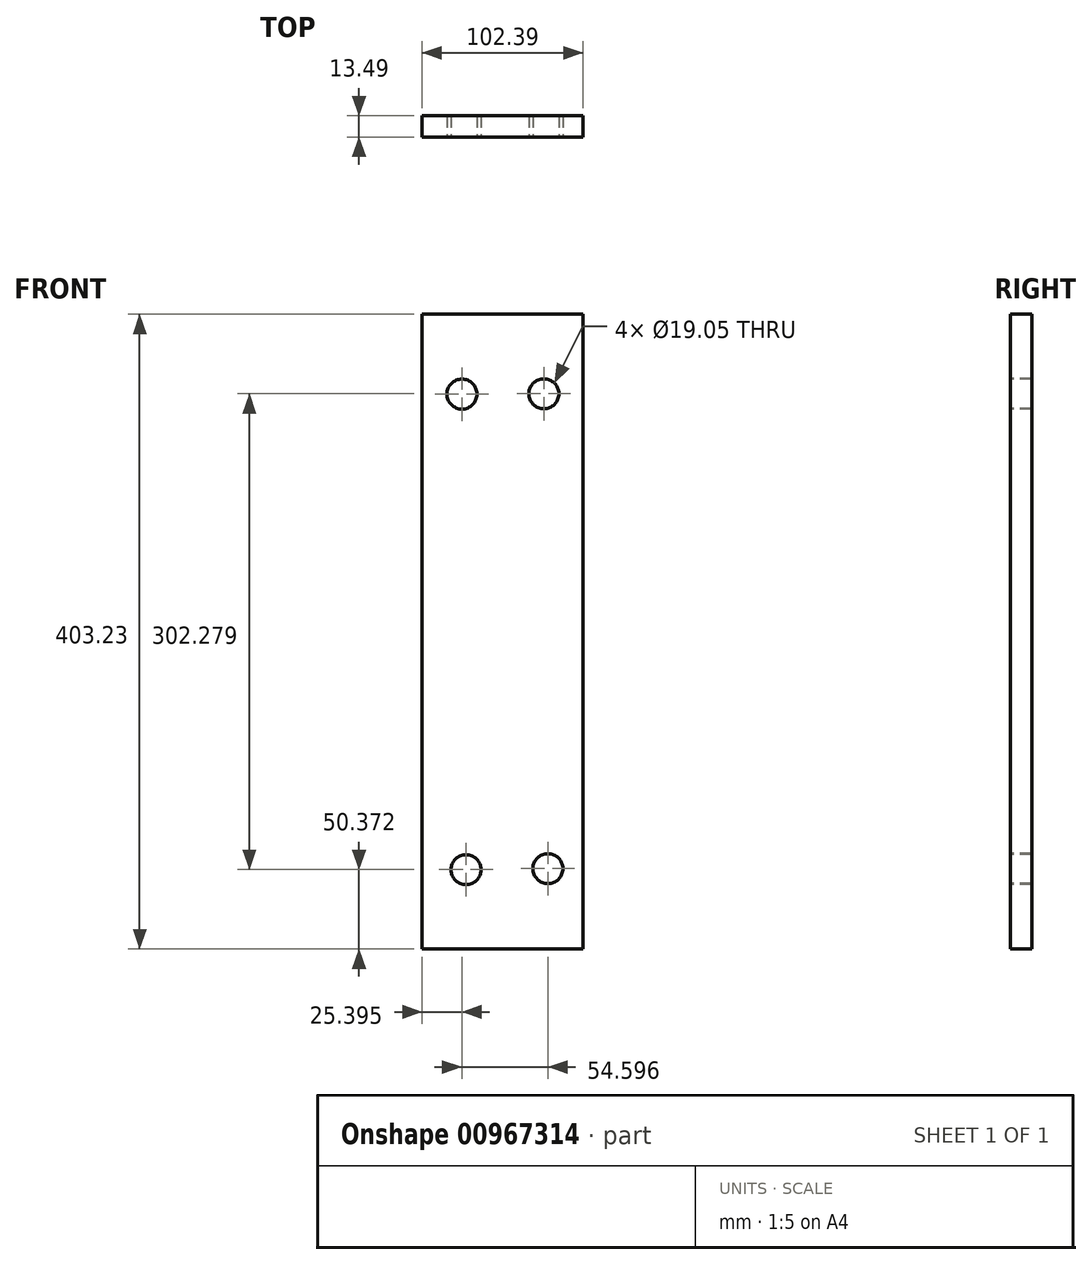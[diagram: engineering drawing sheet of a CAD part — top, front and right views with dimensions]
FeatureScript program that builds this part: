
annotation { "Feature Type Name" : "Feature", "Feature Type Description" : "" }
export const myFeature = defineFeature(function(context is Context, id is Id, definition is map)
    precondition{}
    {
        {
            var Q0;
            Q0=qCreatedBy(makeId("Front.planeOp"),FACE);
            var sketch = newSketch(context, id + "F0", { "sketchPlane" : qUnion([Q0])});
            skLineSegment(sketch, "E0.bottom", {"start": v(-52.91, 320.28) * mm, "end": v(49.48, 320.28) * mm});
            skLineSegment(sketch, "E0.top", {"start": v(-52.91, -82.95) * mm, "end": v(49.48, -82.95) * mm});
            skLineSegment(sketch, "E0.left", {"start": v(-52.91, 320.28) * mm, "end": v(-52.91, -82.95) * mm});
            skLineSegment(sketch, "E0.right", {"start": v(49.48, 320.28) * mm, "end": v(49.48, -82.95) * mm});
            skSolve(sketch);
        }
        {
            var Q0;
            Q0 = qSketchRegion(id + "F0", true);
            extrude(context, id + "F1", {"entities" : qUnion([Q0]), "depth" : 13.5 * mm, "offsetDistance" : 25.4 * mm});
        }
        {
            var Q0;
            Q0=makeQuery(id+"F1.opExtrude","CAP_FACE",FACE,{"disambiguationData":[OSD([sQuery(id+"F0.wireOp",EDGE,"E0.bottom"),sQuery(id+"F0.wireOp",EDGE,"E0.top"),sQuery(id+"F0.wireOp",EDGE,"E0.left"),sQuery(id+"F0.wireOp",EDGE,"E0.right")])],"isStart":false});
            var sketch = newSketch(context, id + "F2", { "sketchPlane" : qUnion([Q0])});
            skCircle(sketch, "E1", {"center": v(-27.51, 269.48) * mm, "radius": 9.53 * mm});
            skLineSegment(sketch, "E2", {"start": v(-52.91, 118.67) * mm, "end": v(49.48, 118.67) * mm, "construction": true});
            skLineSegment(sketch, "E3", {"start": v(-1.72, 320.28) * mm, "end": v(0, -82.95) * mm, "construction": true});
            skCircle(sketch, "E4.MirrorC", {"center": v(24.51, 269.7) * mm, "radius": 9.53 * mm});
            skLineSegment(sketch, "E5.MirrorCS", {"start": v(51.2, 119.11) * mm, "end": v(-51.2, 118.24) * mm, "construction": true});
            skCircle(sketch, "E6.MirrorC", {"center": v(-24.94, -32.58) * mm, "radius": 9.53 * mm});
            skCircle(sketch, "E7.MirrorC", {"center": v(27.08, -31.91) * mm, "radius": 9.53 * mm});
            skSolve(sketch);
        }
        {
            var Q0;
            Q0 = qSketchRegion(id + "F2", true);
            extrude(context, id + "F3", {"entities" : qUnion([Q0]), "operationType" : NewBodyOperationType.REMOVE, "endBound" : BoundingType.THROUGH_ALL, "oppositeDirection" : true, "depth" : 25.4 * mm, "offsetDistance" : 25.4 * mm});
        }
    });
